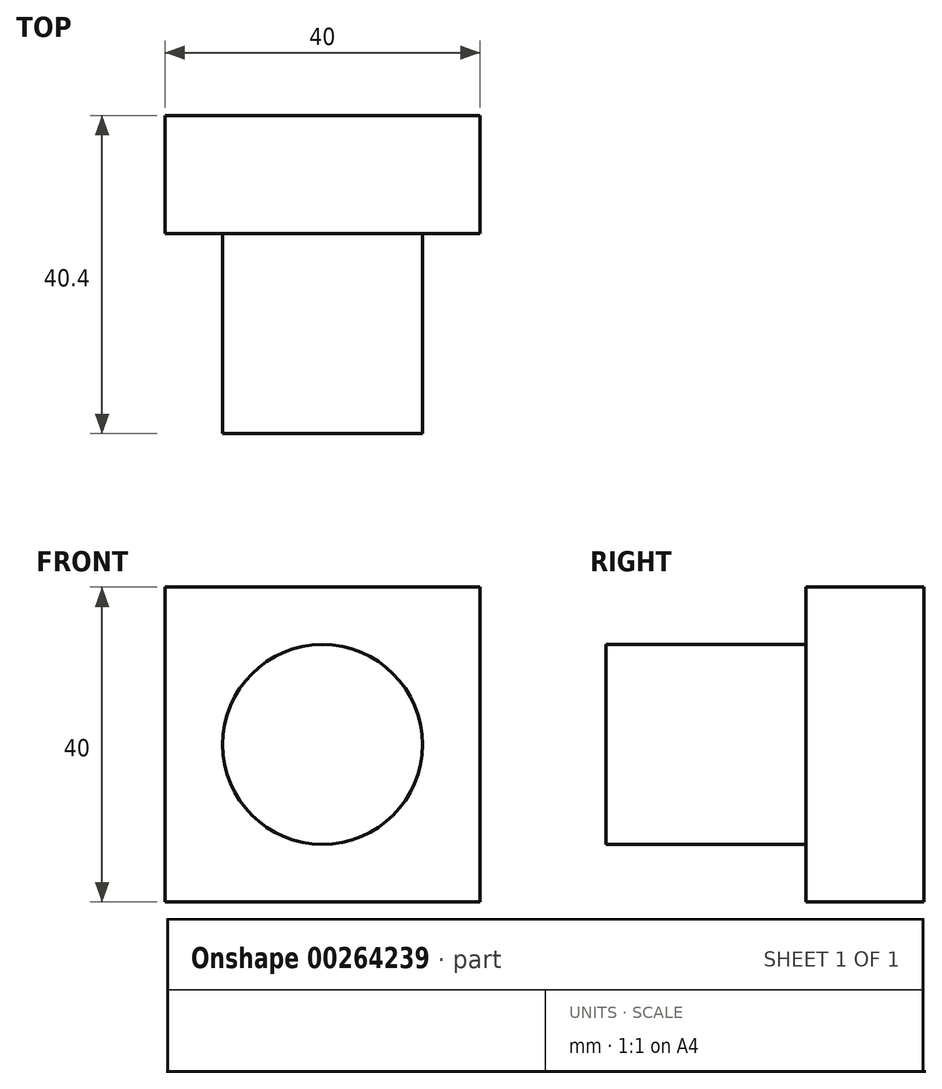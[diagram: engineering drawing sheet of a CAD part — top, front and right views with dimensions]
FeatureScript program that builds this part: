
annotation { "Feature Type Name" : "Feature", "Feature Type Description" : "" }
export const myFeature = defineFeature(function(context is Context, id is Id, definition is map)
    precondition{}
    {
        {
            var Q0;
            Q0=qCreatedBy(makeId("Front.planeOp"),FACE);
            var sketch = newSketch(context, id + "F0", { "sketchPlane" : qUnion([Q0])});
            skLineSegment(sketch, "E0.bottom", {"start": v(7.95, -15.04) * mm, "end": v(-32.05, -15.04) * mm});
            skLineSegment(sketch, "E0.top", {"start": v(7.95, 24.96) * mm, "end": v(-32.05, 24.96) * mm});
            skLineSegment(sketch, "E0.left", {"start": v(7.95, -15.04) * mm, "end": v(7.95, 24.96) * mm});
            skLineSegment(sketch, "E0.right", {"start": v(-32.05, -15.04) * mm, "end": v(-32.05, 24.96) * mm});
            skPoint(sketch, "E0.middle", {"position": v(-12.05, 4.96) * mm});
            skSolve(sketch);
        }
        {
            var Q0;
            Q0=makeQuery(id+"F0.imprint","IMPRINT",FACE,{"disambiguationData":[TD([[makeQuery(id+"F0.imprint","IMPRINT",EDGE,{"derivedFrom":sQuery(id+"F0.wireOp",EDGE,"E0.bottom")}),-1.0]])]});
            extrude(context, id + "F1", {"entities" : qUnion([Q0]), "depth" : 15 * mm});
        }
        {
            var Q0;
            Q0=makeQuery(id+"F0.imprint","IMPRINT",FACE,{"disambiguationData":[TD([[makeQuery(id+"F0.imprint","IMPRINT",EDGE,{"derivedFrom":sQuery(id+"F0.wireOp",EDGE,"E0.bottom")}),-1.0]])]});
            extrude(context, id + "F2", {"entities" : qUnion([Q0]), "depth" : 15 * mm});
        }
        {
            var Q0;
            Q0=makeQuery(id+"F1.opExtrude","CAP_FACE",FACE,{"disambiguationData":[OSD([sQuery(id+"F0.wireOp",EDGE,"E0.bottom"),sQuery(id+"F0.wireOp",EDGE,"E0.top"),sQuery(id+"F0.wireOp",EDGE,"E0.left"),sQuery(id+"F0.wireOp",EDGE,"E0.right")])],"isStart":false});
            var sketch = newSketch(context, id + "F3", { "sketchPlane" : qUnion([Q0])});
            skCircle(sketch, "E1", {"center": v(-12.05, 4.96) * mm, "radius": 12.7 * mm});
            skPoint(sketch, "E1.centerSnap0", {"position": v(-12.05, -15.04) * mm});
            skSolve(sketch);
        }
        {
            var Q0;
            Q0 = qSketchRegion(id + "F3", true);
            extrude(context, id + "F4", {"entities" : qUnion([Q0]), "depth" : 25.4 * mm});
        }
    });
